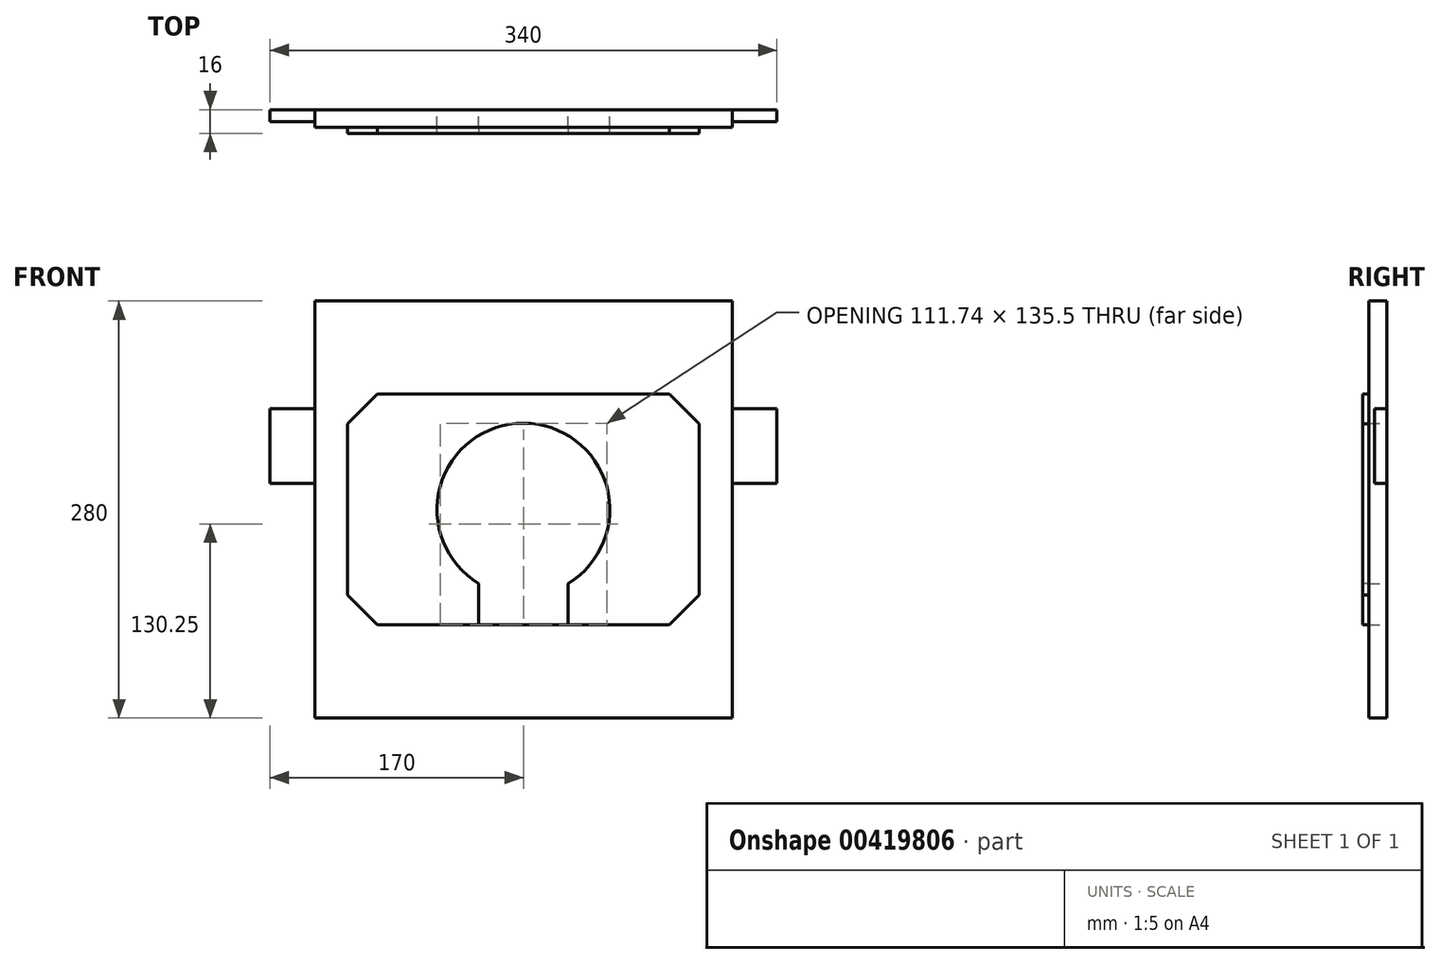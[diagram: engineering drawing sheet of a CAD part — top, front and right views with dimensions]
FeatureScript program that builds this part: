
annotation { "Feature Type Name" : "Feature", "Feature Type Description" : "" }
export const myFeature = defineFeature(function(context is Context, id is Id, definition is map)
    precondition{}
    {
        {
            var Q0;
            Q0=qCreatedBy(makeId("Front.planeOp"),FACE);
            var sketch = newSketch(context, id + "F0", { "sketchPlane" : qUnion([Q0])});
            skLineSegment(sketch, "E0.bottom", {"start": v(140, -140) * mm, "end": v(-140, -140) * mm});
            skLineSegment(sketch, "E0.top", {"start": v(140, 140) * mm, "end": v(-140, 140) * mm});
            skLineSegment(sketch, "E0.left", {"start": v(140, -140) * mm, "end": v(140, 140) * mm});
            skLineSegment(sketch, "E0.right", {"start": v(-140, -140) * mm, "end": v(-140, 140) * mm});
            skPoint(sketch, "E0.middle", {"position": v(0, 0) * mm});
            skCircle(sketch, "E1", {"center": v(0, 0) * mm, "radius": 58 * mm});
            skLineSegment(sketch, "E2", {"start": v(-30, -49.64) * mm, "end": v(-30, -77.5) * mm});
            skLineSegment(sketch, "E3.MirrorCS", {"start": v(30, -49.64) * mm, "end": v(30, -77.5) * mm});
            skLineSegment(sketch, "E4", {"start": v(-30, -77.5) * mm, "end": v(30, -77.5) * mm});
            skSolve(sketch);
        }
        {
            var Q0;
            Q0=makeQuery(id+"F0.imprint","IMPRINT",FACE,{"disambiguationData":[TD([[makeQuery(id+"F0.imprint","IMPRINT",EDGE,{"derivedFrom":sQuery(id+"F0.wireOp",EDGE,"E0.bottom")}),-1.0]])]});
            extrude(context, id + "F1", {"entities" : qUnion([Q0]), "depth" : 12 * mm});
        }
        {
            var Q0;
            Q0=makeQuery(id+"F1.opExtrude","CAP_FACE",FACE,{"disambiguationData":[OSD([sQuery(id+"F0.wireOp",EDGE,"E0.bottom"),sQuery(id+"F0.wireOp",EDGE,"E0.top"),sQuery(id+"F0.wireOp",EDGE,"E0.left"),sQuery(id+"F0.wireOp",EDGE,"E0.right"),sQuery(id+"F0.wireOp",EDGE,"E1")])],"isStart":false});
            var sketch = newSketch(context, id + "F2", { "sketchPlane" : qUnion([Q0])});
            skCircle(sketch, "E5", {"center": v(0, 0) * mm, "radius": 58 * mm});
            skLineSegment(sketch, "E6.bottom", {"start": v(118, -77.5) * mm, "end": v(-118, -77.5) * mm});
            skLineSegment(sketch, "E6.top", {"start": v(118, 77.5) * mm, "end": v(-118, 77.5) * mm});
            skLineSegment(sketch, "E6.left", {"start": v(118, -77.5) * mm, "end": v(118, 77.5) * mm});
            skLineSegment(sketch, "E6.right", {"start": v(-118, -77.5) * mm, "end": v(-118, 77.5) * mm});
            skSolve(sketch);
        }
        {
            var Q0;
            Q0=qSketchRegion(id+"F2",true);
            extrude(context, id + "F3", {"entities" : qUnion([Q0]), "depth" : 4 * mm});
        }
        {
            var Q0;
            Q0=makeQuery(id+"F3.opExtrude","SWEPT_EDGE",EDGE,{"disambiguationData":[OSD([sQuery(id+"F2.wireOp",EDGE,"E6.bottom"),sQuery(id+"F2.wireOp",EDGE,"E6.left")])]});
            var Q1;
            Q1=makeQuery(id+"F3.opExtrude","SWEPT_EDGE",EDGE,{"disambiguationData":[OSD([sQuery(id+"F2.wireOp",EDGE,"E6.bottom"),sQuery(id+"F2.wireOp",EDGE,"E6.right")])]});
            var Q2;
            Q2=makeQuery(id+"F3.opExtrude","SWEPT_EDGE",EDGE,{"disambiguationData":[OSD([sQuery(id+"F2.wireOp",EDGE,"E6.top"),sQuery(id+"F2.wireOp",EDGE,"E6.left")])]});
            var Q3;
            Q3=makeQuery(id+"F3.opExtrude","SWEPT_EDGE",EDGE,{"disambiguationData":[OSD([sQuery(id+"F2.wireOp",EDGE,"E6.top"),sQuery(id+"F2.wireOp",EDGE,"E6.right")])]});
            chamfer(context, id + "F4", {"entities" : qUnion([Q0, Q1, Q2, Q3]), "width" : 20 * mm, "tangentPropagation" : true});
        }
        {
            var Q0;
            Q0=makeQuery(id+"F1.opExtrude","CAP_FACE",FACE,{"disambiguationData":[OSD([sQuery(id+"F0.wireOp",EDGE,"E0.bottom"),sQuery(id+"F0.wireOp",EDGE,"E0.top"),sQuery(id+"F0.wireOp",EDGE,"E0.left"),sQuery(id+"F0.wireOp",EDGE,"E0.right"),sQuery(id+"F0.wireOp",EDGE,"E1")])],"isStart":true});
            var sketch = newSketch(context, id + "F5", { "sketchPlane" : qUnion([Q0])});
            skLineSegment(sketch, "E7.bottom", {"start": v(-170, 67.65) * mm, "end": v(-140, 67.65) * mm});
            skLineSegment(sketch, "E7.top", {"start": v(-170, 17.65) * mm, "end": v(-140, 17.65) * mm});
            skLineSegment(sketch, "E7.left", {"start": v(-170, 67.65) * mm, "end": v(-170, 17.65) * mm});
            skLineSegment(sketch, "E7.right", {"start": v(-140, 67.65) * mm, "end": v(-140, 17.65) * mm});
            skLineSegment(sketch, "E8", {"start": v(0, 84.07) * mm, "end": v(0, -91.42) * mm, "construction": true});
            skLineSegment(sketch, "E9.MirrorCS", {"start": v(170, 67.65) * mm, "end": v(140, 67.65) * mm});
            skLineSegment(sketch, "E10.MirrorCS", {"start": v(170, 67.65) * mm, "end": v(170, 17.65) * mm});
            skLineSegment(sketch, "E11.MirrorCS", {"start": v(170, 17.65) * mm, "end": v(140, 17.65) * mm});
            skLineSegment(sketch, "E12.MirrorCS", {"start": v(140, 67.65) * mm, "end": v(140, 17.65) * mm});
            skSolve(sketch);
        }
        {
            var Q0;
            Q0=qSketchRegion(id+"F5",true);
            extrude(context, id + "F6", {"entities" : qUnion([Q0]), "operationType" : NewBodyOperationType.ADD, "depth" : -8 * mm});
        }
        {
            var Q0;
            Q0=makeQuery(id+"F3.opExtrude","CAP_FACE",FACE,{"disambiguationData":[OSD([sQuery(id+"F2.wireOp",EDGE,"E5"),sQuery(id+"F2.wireOp",EDGE,"E6.bottom"),sQuery(id+"F2.wireOp",EDGE,"E6.top"),sQuery(id+"F2.wireOp",EDGE,"E6.left"),sQuery(id+"F2.wireOp",EDGE,"E6.right")])],"isStart":false});
            var sketch = newSketch(context, id + "F7", { "sketchPlane" : qUnion([Q0])});
            skLineSegment(sketch, "E13", {"start": v(-30, -49.64) * mm, "end": v(-30, -77.5) * mm});
            skLineSegment(sketch, "E14.MirrorCS", {"start": v(30, -49.64) * mm, "end": v(30, -77.5) * mm});
            skSolve(sketch);
        }
        {
            var Q0;
            {var subQ0=sQuery(id+"F7.wireOp",EDGE,"E13");Q0=makeQuery(id+"F7.imprint","IMPRINT",FACE,{"disambiguationData":[TD([[makeQuery(id+"F7.imprint","IMPRINT",EDGE,{"derivedFrom":subQ0}),1.0]])]});}
            extrude(context, id + "F8", {"entities" : qUnion([Q0]), "operationType" : NewBodyOperationType.REMOVE, "endBound" : BoundingType.THROUGH_ALL, "oppositeDirection" : true, "depth" : 25 * mm});
        }
        {
            var Q0;
            {var subQ0=sQuery(id+"F0.wireOp",EDGE,"E2");Q0=makeQuery(id+"F0.imprint","IMPRINT",FACE,{"disambiguationData":[TD([[makeQuery(id+"F0.imprint","IMPRINT",EDGE,{"derivedFrom":subQ0}),1.0]])]});}
            extrude(context, id + "F9", {"entities" : qUnion([Q0]), "operationType" : NewBodyOperationType.REMOVE, "endBound" : BoundingType.THROUGH_ALL, "oppositeDirection" : true, "depth" : 25 * mm});
        }
    });
